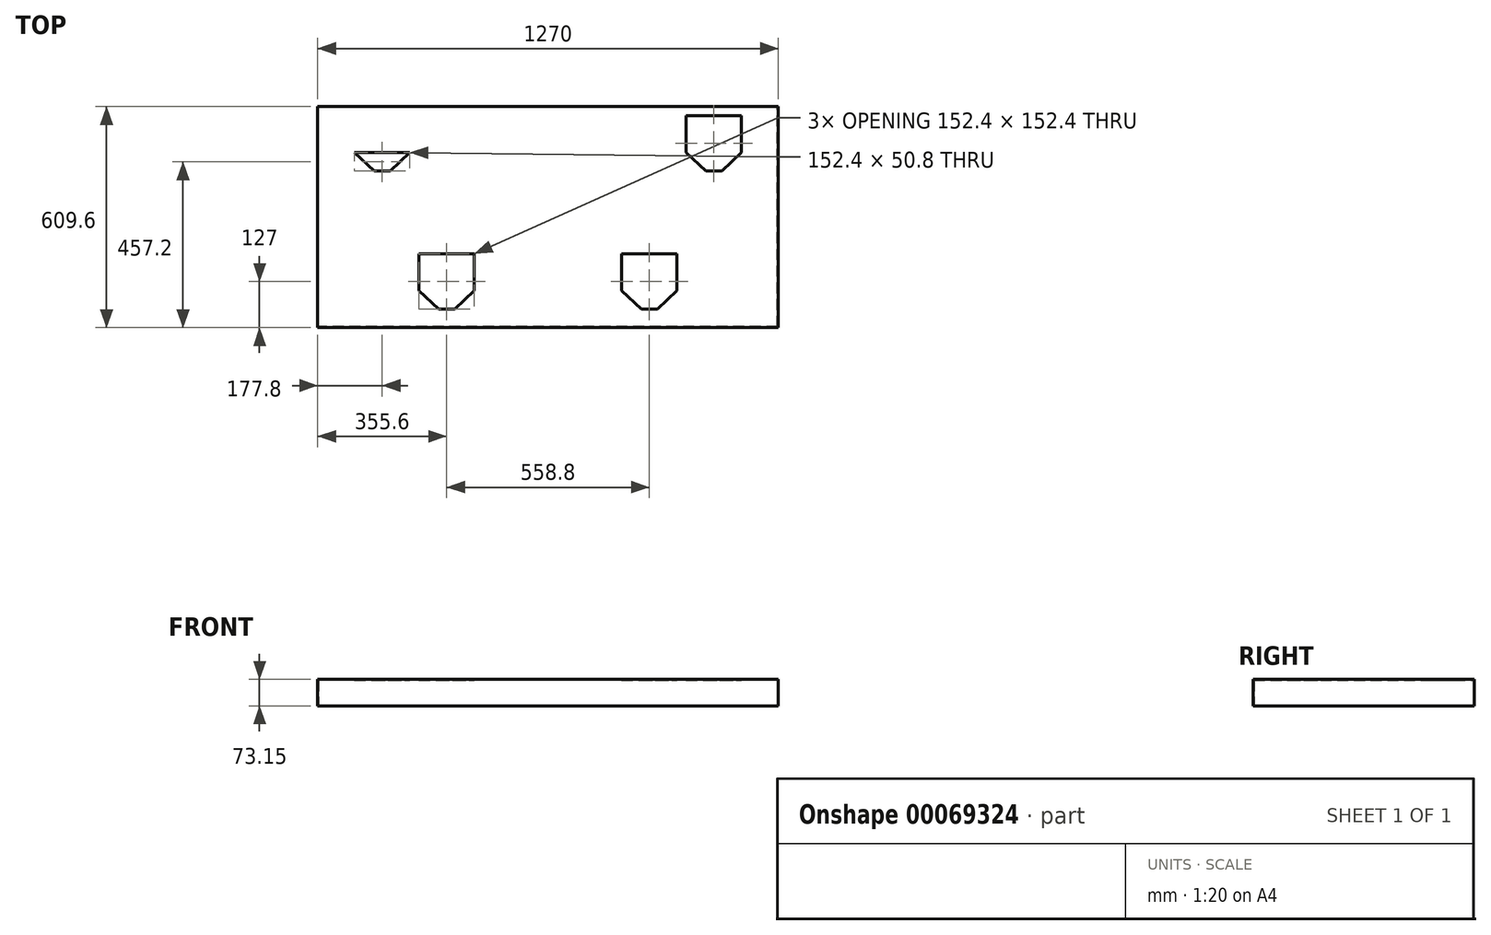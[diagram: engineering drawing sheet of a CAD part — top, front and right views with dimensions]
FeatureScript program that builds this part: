
annotation { "Feature Type Name" : "Feature", "Feature Type Description" : "" }
export const myFeature = defineFeature(function(context is Context, id is Id, definition is map)
    precondition{}
    {
        {
            var Q0;
            Q0=qCreatedBy(makeId("Top.planeOp"),FACE);
            var sketch = newSketch(context, id + "F0", { "sketchPlane" : qUnion([Q0])});
            skLineSegment(sketch, "E0.rect.bottom", {"start": v(635, -304.8) * mm, "end": v(-635, -304.8) * mm});
            skLineSegment(sketch, "E0.rect.top", {"start": v(635, 304.8) * mm, "end": v(-635, 304.8) * mm});
            skLineSegment(sketch, "E0.rect.left", {"start": v(635, -304.8) * mm, "end": v(635, 304.8) * mm});
            skLineSegment(sketch, "E0.rect.right", {"start": v(-635, -304.8) * mm, "end": v(-635, 304.8) * mm});
            skPoint(sketch, "E0.rect.middle", {"position": v(0, 0) * mm});
            skSolve(sketch);
        }
        {
            var Q0;
            Q0=makeQuery(id+"F0.imprint","IMPRINT",FACE,{"disambiguationData":[TD([[makeQuery(id+"F0.imprint","IMPRINT",EDGE,{"derivedFrom":sQuery(id+"F0.wireOp",EDGE,"E0.rect.bottom")}),-1.0]])]});
            extrude(context, id + "F1", {"entities" : qUnion([Q0]), "depth" : 73.15 * mm});
        }
        {
            var Q0;
            Q0=makeQuery(id+"F1.opExtrude","CAP_FACE",FACE,{"disambiguationData":[OSD([sQuery(id+"F0.wireOp",EDGE,"E0.rect.bottom"),sQuery(id+"F0.wireOp",EDGE,"E0.rect.top"),sQuery(id+"F0.wireOp",EDGE,"E0.rect.left"),sQuery(id+"F0.wireOp",EDGE,"E0.rect.right")])],"isStart":true});
            shell(context, id + "F2", {"entities" : qUnion([Q0]), "thickness" : 2.67 * mm});
        }
        {
            var Q0;
            Q0=makeQuery(id+"F1.opExtrude","CAP_FACE",FACE,{"disambiguationData":[OSD([sQuery(id+"F0.wireOp",EDGE,"E0.rect.bottom"),sQuery(id+"F0.wireOp",EDGE,"E0.rect.top"),sQuery(id+"F0.wireOp",EDGE,"E0.rect.left"),sQuery(id+"F0.wireOp",EDGE,"E0.rect.right")])],"isStart":false});
            var sketch = newSketch(context, id + "F3", { "sketchPlane" : qUnion([Q0])});
            skLineSegment(sketch, "E1.rect.bottom", {"start": v(-381, 101.6) * mm, "end": v(-533.4, 101.6) * mm});
            skLineSegment(sketch, "E1.rect.top", {"start": v(-381, 279.4) * mm, "end": v(-533.4, 279.4) * mm});
            skLineSegment(sketch, "E1.rect.left", {"start": v(-381, 101.6) * mm, "end": v(-381, 279.4) * mm});
            skLineSegment(sketch, "E1.rect.right", {"start": v(-533.4, 101.6) * mm, "end": v(-533.4, 279.4) * mm});
            skPoint(sketch, "E1.rect.middle", {"position": v(-457.2, 190.5) * mm});
            skLineSegment(sketch, "E2.bottom", {"start": v(-479.43, 101.6) * mm, "end": v(-434.98, 101.6) * mm});
            skLineSegment(sketch, "E2.top", {"start": v(-479.43, 127) * mm, "end": v(-434.98, 127) * mm});
            skLineSegment(sketch, "E2.left", {"start": v(-479.43, 101.6) * mm, "end": v(-479.43, 127) * mm});
            skLineSegment(sketch, "E2.right", {"start": v(-434.98, 101.6) * mm, "end": v(-434.98, 127) * mm});
            skLineSegment(sketch, "E3.bottom", {"start": v(-533.4, 279.4) * mm, "end": v(-381, 279.4) * mm});
            skLineSegment(sketch, "E3.top", {"start": v(-533.4, 177.8) * mm, "end": v(-381, 177.8) * mm});
            skLineSegment(sketch, "E3.left", {"start": v(-533.4, 279.4) * mm, "end": v(-533.4, 177.8) * mm});
            skLineSegment(sketch, "E3.right", {"start": v(-381, 279.4) * mm, "end": v(-381, 177.8) * mm});
            skLineSegment(sketch, "E4", {"start": v(-533.4, 177.8) * mm, "end": v(-479.43, 127) * mm});
            skLineSegment(sketch, "E5", {"start": v(-434.98, 127) * mm, "end": v(-381, 177.8) * mm});
            skLineSegment(sketch, "E6.rect.bottom", {"start": v(-203.2, -279.4) * mm, "end": v(-355.6, -279.4) * mm});
            skLineSegment(sketch, "E7.top", {"start": v(-355.6, -203.2) * mm, "end": v(-203.2, -203.2) * mm});
            skLineSegment(sketch, "E6.rect.right", {"start": v(-355.6, -279.4) * mm, "end": v(-355.6, -101.6) * mm});
            skLineSegment(sketch, "E8.bottom", {"start": v(-301.63, -279.4) * mm, "end": v(-257.18, -279.4) * mm});
            skLineSegment(sketch, "E8.top", {"start": v(-301.63, -254) * mm, "end": v(-257.18, -254) * mm});
            skLineSegment(sketch, "E8.left", {"start": v(-301.63, -279.4) * mm, "end": v(-301.63, -254) * mm});
            skLineSegment(sketch, "E7.bottom", {"start": v(-355.6, -101.6) * mm, "end": v(-203.2, -101.6) * mm});
            skLineSegment(sketch, "E7.right", {"start": v(-203.2, -101.6) * mm, "end": v(-203.2, -203.2) * mm});
            skLineSegment(sketch, "E9", {"start": v(-355.6, -203.2) * mm, "end": v(-301.62, -254) * mm});
            skLineSegment(sketch, "E6.rect.left", {"start": v(-203.2, -279.4) * mm, "end": v(-203.2, -101.6) * mm});
            skLineSegment(sketch, "E7.left", {"start": v(-355.6, -101.6) * mm, "end": v(-355.6, -203.2) * mm});
            skLineSegment(sketch, "E8.right", {"start": v(-257.18, -279.4) * mm, "end": v(-257.18, -254) * mm});
            skPoint(sketch, "E6.rect.middle", {"position": v(-279.4, -190.5) * mm});
            skLineSegment(sketch, "E10", {"start": v(-257.18, -254) * mm, "end": v(-203.2, -203.2) * mm});
            skLineSegment(sketch, "E6.rect.top", {"start": v(-203.2, -101.6) * mm, "end": v(-355.6, -101.6) * mm});
            skLineSegment(sketch, "E11.rect.bottom", {"start": v(355.6, -279.4) * mm, "end": v(203.2, -279.4) * mm});
            skLineSegment(sketch, "E12.top", {"start": v(203.2, -203.2) * mm, "end": v(355.6, -203.2) * mm});
            skLineSegment(sketch, "E11.rect.right", {"start": v(203.2, -279.4) * mm, "end": v(203.2, -101.6) * mm});
            skLineSegment(sketch, "E13.bottom", {"start": v(257.18, -279.4) * mm, "end": v(301.63, -279.4) * mm});
            skLineSegment(sketch, "E13.top", {"start": v(257.18, -254) * mm, "end": v(301.63, -254) * mm});
            skLineSegment(sketch, "E13.left", {"start": v(257.18, -279.4) * mm, "end": v(257.18, -254) * mm});
            skLineSegment(sketch, "E12.bottom", {"start": v(203.2, -101.6) * mm, "end": v(355.6, -101.6) * mm});
            skLineSegment(sketch, "E12.right", {"start": v(355.6, -101.6) * mm, "end": v(355.6, -203.2) * mm});
            skLineSegment(sketch, "E14", {"start": v(203.2, -203.2) * mm, "end": v(257.18, -254) * mm});
            skLineSegment(sketch, "E11.rect.left", {"start": v(355.6, -279.4) * mm, "end": v(355.6, -101.6) * mm});
            skLineSegment(sketch, "E12.left", {"start": v(203.2, -101.6) * mm, "end": v(203.2, -203.2) * mm});
            skLineSegment(sketch, "E13.right", {"start": v(301.63, -279.4) * mm, "end": v(301.63, -254) * mm});
            skPoint(sketch, "E11.rect.middle", {"position": v(279.4, -190.5) * mm});
            skLineSegment(sketch, "E15", {"start": v(301.63, -254) * mm, "end": v(355.6, -203.2) * mm});
            skLineSegment(sketch, "E11.rect.top", {"start": v(355.6, -101.6) * mm, "end": v(203.2, -101.6) * mm});
            skLineSegment(sketch, "E16.rect.bottom", {"start": v(533.4, 101.6) * mm, "end": v(381, 101.6) * mm});
            skLineSegment(sketch, "E17.top", {"start": v(381, 177.8) * mm, "end": v(533.4, 177.8) * mm});
            skLineSegment(sketch, "E16.rect.right", {"start": v(381, 101.6) * mm, "end": v(381, 279.4) * mm});
            skLineSegment(sketch, "E18.bottom", {"start": v(434.98, 101.6) * mm, "end": v(479.43, 101.6) * mm});
            skLineSegment(sketch, "E18.top", {"start": v(434.98, 127) * mm, "end": v(479.43, 127) * mm});
            skLineSegment(sketch, "E18.left", {"start": v(434.98, 101.6) * mm, "end": v(434.98, 127) * mm});
            skLineSegment(sketch, "E17.bottom", {"start": v(381, 279.4) * mm, "end": v(533.4, 279.4) * mm});
            skLineSegment(sketch, "E17.right", {"start": v(533.4, 279.4) * mm, "end": v(533.4, 177.8) * mm});
            skLineSegment(sketch, "E19", {"start": v(381, 177.8) * mm, "end": v(434.98, 127) * mm});
            skLineSegment(sketch, "E16.rect.left", {"start": v(533.4, 101.6) * mm, "end": v(533.4, 279.4) * mm});
            skLineSegment(sketch, "E17.left", {"start": v(381, 279.4) * mm, "end": v(381, 177.8) * mm});
            skLineSegment(sketch, "E18.right", {"start": v(479.43, 101.6) * mm, "end": v(479.43, 127) * mm});
            skPoint(sketch, "E16.rect.middle", {"position": v(457.2, 190.5) * mm});
            skLineSegment(sketch, "E20", {"start": v(479.42, 127) * mm, "end": v(533.4, 177.8) * mm});
            skLineSegment(sketch, "E16.rect.top", {"start": v(533.4, 279.4) * mm, "end": v(381, 279.4) * mm});
            skSolve(sketch);
        }
        {
            var Q0;
            Q0=makeQuery(id+"F3.imprint","IMPRINT",FACE,{"disambiguationData":[TD([[makeQuery(id+"F3.imprint","IMPRINT",EDGE,{"derivedFrom":sQuery(id+"F3.wireOp",EDGE,"E3.bottom")}),-1.0]])]});
            var Q1;
            Q1=makeQuery(id+"F3.imprint","IMPRINT",FACE,{"disambiguationData":[TD([[makeQuery(id+"F3.imprint","IMPRINT",EDGE,{"derivedFrom":sQuery(id+"F3.wireOp",EDGE,"E2.top")}),1.0]])]});
            var Q2;
            Q2=makeQuery(id+"F3.imprint","IMPRINT",FACE,{"disambiguationData":[TD([[makeQuery(id+"F3.imprint","IMPRINT",EDGE,{"derivedFrom":sQuery(id+"F3.wireOp",EDGE,"E2.bottom")}),1.0]])]});
            var Q3;
            {var subQ0=sQuery(id+"F3.wireOp",EDGE,"E7.top");Q3=makeQuery(id+"F3.imprint","IMPRINT",FACE,{"disambiguationData":[TD([[makeQuery(id+"F3.imprint","IMPRINT",EDGE,{"derivedFrom":subQ0}),1.0]])]});}
            var Q4;
            Q4=makeQuery(id+"F3.imprint","IMPRINT",FACE,{"disambiguationData":[TD([[makeQuery(id+"F3.imprint","IMPRINT",EDGE,{"derivedFrom":sQuery(id+"F3.wireOp",EDGE,"E7.top")}),-1.0]])]});
            var Q5;
            Q5=makeQuery(id+"F3.imprint","IMPRINT",FACE,{"disambiguationData":[TD([[makeQuery(id+"F3.imprint","IMPRINT",EDGE,{"derivedFrom":sQuery(id+"F3.wireOp",EDGE,"E8.bottom")}),1.0]])]});
            var Q6;
            {var subQ0=sQuery(id+"F3.wireOp",EDGE,"E12.top");Q6=makeQuery(id+"F3.imprint","IMPRINT",FACE,{"disambiguationData":[TD([[makeQuery(id+"F3.imprint","IMPRINT",EDGE,{"derivedFrom":subQ0}),1.0]])]});}
            var Q7;
            Q7=makeQuery(id+"F3.imprint","IMPRINT",FACE,{"disambiguationData":[TD([[makeQuery(id+"F3.imprint","IMPRINT",EDGE,{"derivedFrom":sQuery(id+"F3.wireOp",EDGE,"E12.top")}),-1.0]])]});
            var Q8;
            Q8=makeQuery(id+"F3.imprint","IMPRINT",FACE,{"disambiguationData":[TD([[makeQuery(id+"F3.imprint","IMPRINT",EDGE,{"derivedFrom":sQuery(id+"F3.wireOp",EDGE,"E13.bottom")}),1.0]])]});
            var Q9;
            {var subQ0=sQuery(id+"F3.wireOp",EDGE,"E17.top");Q9=makeQuery(id+"F3.imprint","IMPRINT",FACE,{"disambiguationData":[TD([[makeQuery(id+"F3.imprint","IMPRINT",EDGE,{"derivedFrom":subQ0}),1.0]])]});}
            var Q10;
            Q10=makeQuery(id+"F3.imprint","IMPRINT",FACE,{"disambiguationData":[TD([[makeQuery(id+"F3.imprint","IMPRINT",EDGE,{"derivedFrom":sQuery(id+"F3.wireOp",EDGE,"E17.top")}),-1.0]])]});
            var Q11;
            Q11=makeQuery(id+"F3.imprint","IMPRINT",FACE,{"disambiguationData":[TD([[makeQuery(id+"F3.imprint","IMPRINT",EDGE,{"derivedFrom":sQuery(id+"F3.wireOp",EDGE,"E18.bottom")}),1.0]])]});
            extrude(context, id + "F4", {"entities" : qUnion([Q0, Q1, Q2, Q3, Q4, Q5, Q6, Q7, Q8, Q9, Q10, Q11]), "operationType" : NewBodyOperationType.REMOVE, "endBound" : BoundingType.THROUGH_ALL, "oppositeDirection" : true, "depth" : 25.4 * mm});
        }
    });
